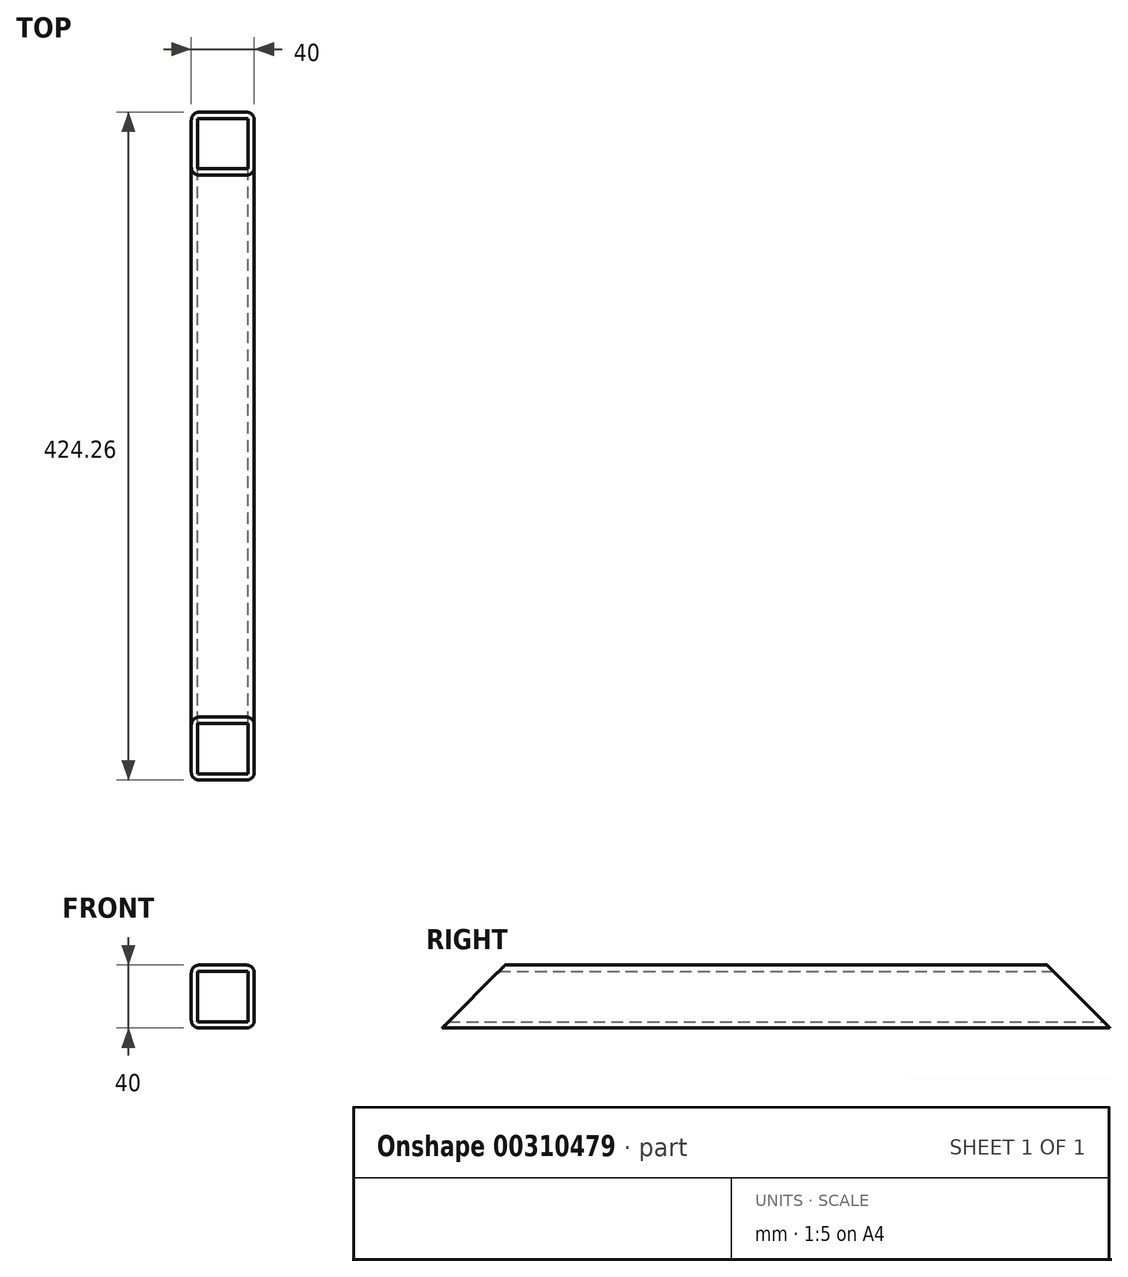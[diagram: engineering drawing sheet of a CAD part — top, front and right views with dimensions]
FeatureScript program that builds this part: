
annotation { "Feature Type Name" : "Feature", "Feature Type Description" : "" }
export const myFeature = defineFeature(function(context is Context, id is Id, definition is map)
    precondition{}
    {
        {
            var Q0;
            Q0=qCreatedBy(makeId("Front.planeOp"),FACE);
            var sketch = newSketch(context, id + "F0", { "sketchPlane" : qUnion([Q0])});
            skLineSegment(sketch, "E0.bottom", {"start": v(15, -20) * mm, "end": v(-15, -20) * mm});
            skLineSegment(sketch, "E0.top", {"start": v(15, 20) * mm, "end": v(-15, 20) * mm});
            skLineSegment(sketch, "E0.left", {"start": v(20, -15) * mm, "end": v(20, 15) * mm});
            skLineSegment(sketch, "E0.right", {"start": v(-20, -15) * mm, "end": v(-20, 15) * mm});
            skPoint(sketch, "E0.middle", {"position": v(0, 0) * mm});
            skPoint(sketch, "E1.visualSharp", {"position": v(-20, 20) * mm});
            skArc(sketch, "E1.filletArc", {"start": v(-15, 20) * mm, "mid": v(-18.54, 18.54) * mm, "end": v(-20, 15) * mm});
            skPoint(sketch, "E2.visualSharp", {"position": v(20, 20) * mm});
            skArc(sketch, "E2.filletArc", {"start": v(20, 15) * mm, "mid": v(18.54, 18.54) * mm, "end": v(15, 20) * mm});
            skPoint(sketch, "E3.visualSharp", {"position": v(20, -20) * mm});
            skArc(sketch, "E3.filletArc", {"start": v(15, -20) * mm, "mid": v(18.54, -18.54) * mm, "end": v(20, -15) * mm});
            skPoint(sketch, "E4.visualSharp", {"position": v(-20, -20) * mm});
            skArc(sketch, "E4.filletArc", {"start": v(-20, -15) * mm, "mid": v(-18.54, -18.54) * mm, "end": v(-15, -20) * mm});
            skLineSegment(sketch, "E5.0", {"start": v(-16, -16) * mm, "end": v(-16, 16) * mm});
            skLineSegment(sketch, "E5.1", {"start": v(16, -16) * mm, "end": v(-16, -16) * mm});
            skLineSegment(sketch, "E5.2", {"start": v(16, -16) * mm, "end": v(16, 16) * mm});
            skLineSegment(sketch, "E5.3", {"start": v(16, 16) * mm, "end": v(-16, 16) * mm});
            skSolve(sketch);
        }
        {
            var Q0;
            Q0=makeQuery(id+"F0.imprint","IMPRINT",FACE,{"disambiguationData":[TD([[makeQuery(id+"F0.imprint","IMPRINT",EDGE,{"derivedFrom":sQuery(id+"F0.wireOp",EDGE,"E0.bottom")}),-1.0]])]});
            extrude(context, id + "F1", {"entities" : qUnion([Q0]), "depth" : 424.26 * mm});
        }
        {
            var Q0;
            Q0=makeQuery(id+"F1.opExtrude","CAP_FACE",FACE,{"disambiguationData":[OSD([sQuery(id+"F0.wireOp",EDGE,"E0.bottom"),sQuery(id+"F0.wireOp",EDGE,"E0.top"),sQuery(id+"F0.wireOp",EDGE,"E0.left"),sQuery(id+"F0.wireOp",EDGE,"E0.right"),sQuery(id+"F0.wireOp",EDGE,"E1.filletArc"),sQuery(id+"F0.wireOp",EDGE,"E2.filletArc"),sQuery(id+"F0.wireOp",EDGE,"E3.filletArc"),sQuery(id+"F0.wireOp",EDGE,"E4.filletArc"),sQuery(id+"F0.wireOp",EDGE,"E5.0"),sQuery(id+"F0.wireOp",EDGE,"E5.1"),sQuery(id+"F0.wireOp",EDGE,"E5.2"),sQuery(id+"F0.wireOp",EDGE,"E5.3")])],"isStart":false});
            var sketch = newSketch(context, id + "F2", { "sketchPlane" : qUnion([Q0])});
            skLineSegment(sketch, "E6.bottom", {"start": v(20, -20) * mm, "end": v(-20, -20) * mm});
            skLineSegment(sketch, "E6.top", {"start": v(20, 20) * mm, "end": v(-20, 20) * mm});
            skLineSegment(sketch, "E6.left", {"start": v(20, -20) * mm, "end": v(20, 20) * mm});
            skLineSegment(sketch, "E6.right", {"start": v(-20, -20) * mm, "end": v(-20, 20) * mm});
            skPoint(sketch, "E6.middle", {"position": v(0, 0) * mm});
            skLineSegment(sketch, "E7.bottom", {"start": v(-20, -20) * mm, "end": v(20, -20) * mm});
            skLineSegment(sketch, "E7.top", {"start": v(-20, 37) * mm, "end": v(20, 37) * mm});
            skLineSegment(sketch, "E7.left", {"start": v(-20, -20) * mm, "end": v(-20, 37) * mm});
            skLineSegment(sketch, "E7.right", {"start": v(20, -20) * mm, "end": v(20, 37) * mm});
            skSolve(sketch);
        }
        {
            var Q0;
            {var subQ3=makeQuery(id+"F1.opExtrude","CAP_EDGE",EDGE,{"disambiguationData":[OSD([sQuery(id+"F0.wireOp",EDGE,"E1.filletArc")])],"isStart":false});Q0=makeQuery(id+"F2.imprint","IMPRINT",FACE,{"disambiguationData":[TD([[makeQuery(id+"F2.imprint","IMPRINT",EDGE,{"derivedFrom":subQ3}),1.0]])]});}
            var Q1;
            {var subQ1=makeQuery(id+"F1.opExtrude","CAP_EDGE",EDGE,{"disambiguationData":[OSD([sQuery(id+"F0.wireOp",EDGE,"E2.filletArc")])],"isStart":false});Q1=makeQuery(id+"F2.imprint","IMPRINT",FACE,{"disambiguationData":[TD([[makeQuery(id+"F2.imprint","IMPRINT",EDGE,{"derivedFrom":subQ1}),-1.0]])]});}
            var Q2;
            {var subQ1=makeQuery(id+"F1.opExtrude","CAP_EDGE",EDGE,{"disambiguationData":[OSD([sQuery(id+"F0.wireOp",EDGE,"E1.filletArc")])],"isStart":false});Q2=makeQuery(id+"F2.imprint","IMPRINT",FACE,{"disambiguationData":[TD([[makeQuery(id+"F2.imprint","IMPRINT",EDGE,{"derivedFrom":subQ1}),-1.0]])]});}
            var Q3;
            {var subQ1=makeQuery(id+"F1.opExtrude","CAP_EDGE",EDGE,{"disambiguationData":[OSD([sQuery(id+"F0.wireOp",EDGE,"E3.filletArc")])],"isStart":false});Q3=makeQuery(id+"F2.imprint","IMPRINT",FACE,{"disambiguationData":[TD([[makeQuery(id+"F2.imprint","IMPRINT",EDGE,{"derivedFrom":subQ1}),-1.0]])]});}
            var Q4;
            Q4=makeQuery(id+"F2.imprint","IMPRINT",FACE,{"disambiguationData":[TD([[makeQuery(id+"F2.imprint","IMPRINT",EDGE,{"derivedFrom":makeQuery(id+"F1.opExtrude","CAP_EDGE",EDGE,{"disambiguationData":[OSD([sQuery(id+"F0.wireOp",EDGE,"E5.0")])],"isStart":false})}),-1.0]])]});
            var Q5;
            {var subQ4=sQuery(id+"F2.wireOp",EDGE,"E7.top");Q5=makeQuery(id+"F2.imprint","IMPRINT",FACE,{"disambiguationData":[TD([[makeQuery(id+"F2.imprint","IMPRINT",EDGE,{"derivedFrom":subQ4}),-1.0]])]});}
            var Q6;
            {var subQ1=makeQuery(id+"F1.opExtrude","CAP_EDGE",EDGE,{"disambiguationData":[OSD([sQuery(id+"F0.wireOp",EDGE,"E4.filletArc")])],"isStart":false});Q6=makeQuery(id+"F2.imprint","IMPRINT",FACE,{"disambiguationData":[TD([[makeQuery(id+"F2.imprint","IMPRINT",EDGE,{"derivedFrom":subQ1}),-1.0]])]});}
            var Q7;
            Q7=sQuery(id+"F2.wireOp",EDGE,"E7.bottom");
            revolve(context, id + "F3", {"operationType" : NewBodyOperationType.REMOVE, "entities" : qUnion([Q0, Q1, Q2, Q3, Q4, Q5, Q6]), "axis" : qUnion([Q7]), "revolveType" : RevolveType.ONE_DIRECTION, "oppositeDirection" : true, "angle" : 45 * degree});
        }
        {
            var Q0;
            Q0=makeQuery(id+"F1.opExtrude","CAP_FACE",FACE,{"disambiguationData":[OSD([sQuery(id+"F0.wireOp",EDGE,"E0.bottom"),sQuery(id+"F0.wireOp",EDGE,"E0.top"),sQuery(id+"F0.wireOp",EDGE,"E0.left"),sQuery(id+"F0.wireOp",EDGE,"E0.right"),sQuery(id+"F0.wireOp",EDGE,"E1.filletArc"),sQuery(id+"F0.wireOp",EDGE,"E2.filletArc"),sQuery(id+"F0.wireOp",EDGE,"E3.filletArc"),sQuery(id+"F0.wireOp",EDGE,"E4.filletArc"),sQuery(id+"F0.wireOp",EDGE,"E5.0"),sQuery(id+"F0.wireOp",EDGE,"E5.1"),sQuery(id+"F0.wireOp",EDGE,"E5.2"),sQuery(id+"F0.wireOp",EDGE,"E5.3")])],"isStart":true});
            var sketch = newSketch(context, id + "F4", { "sketchPlane" : qUnion([Q0])});
            skLineSegment(sketch, "E8.bottom", {"start": v(-20, -20) * mm, "end": v(20, -20) * mm});
            skLineSegment(sketch, "E8.top", {"start": v(-20, 37) * mm, "end": v(20, 37) * mm});
            skLineSegment(sketch, "E8.left", {"start": v(-20, -20) * mm, "end": v(-20, 37) * mm});
            skLineSegment(sketch, "E8.right", {"start": v(20, -20) * mm, "end": v(20, 37) * mm});
            skSolve(sketch);
        }
        {
            var Q0;
            {var subQ2=sQuery(id+"F4.wireOp",EDGE,"E8.top");Q0=makeQuery(id+"F4.imprint","IMPRINT",FACE,{"disambiguationData":[TD([[makeQuery(id+"F4.imprint","IMPRINT",EDGE,{"derivedFrom":subQ2}),-1.0]])]});}
            var Q1;
            Q1=makeQuery(id+"F4.imprint","IMPRINT",FACE,{"disambiguationData":[TD([[makeQuery(id+"F4.imprint","IMPRINT",EDGE,{"derivedFrom":makeQuery(id+"F1.opExtrude","CAP_EDGE",EDGE,{"disambiguationData":[OSD([sQuery(id+"F0.wireOp",EDGE,"E5.0")])],"isStart":true})}),1.0]])]});
            var Q2;
            Q2=makeQuery(id+"F4.imprint","IMPRINT",FACE,{"disambiguationData":[TD([[makeQuery(id+"F4.imprint","IMPRINT",EDGE,{"derivedFrom":makeQuery(id+"F1.opExtrude","CAP_EDGE",EDGE,{"disambiguationData":[OSD([sQuery(id+"F0.wireOp",EDGE,"E0.top")])],"isStart":true})}),-1.0]])]});
            var Q3;
            {var subQ1=makeQuery(id+"F1.opExtrude","CAP_EDGE",EDGE,{"disambiguationData":[OSD([sQuery(id+"F0.wireOp",EDGE,"E4.filletArc")])],"isStart":true});Q3=makeQuery(id+"F4.imprint","IMPRINT",FACE,{"disambiguationData":[TD([[makeQuery(id+"F4.imprint","IMPRINT",EDGE,{"derivedFrom":subQ1}),1.0]])]});}
            var Q4;
            {var subQ1=makeQuery(id+"F1.opExtrude","CAP_EDGE",EDGE,{"disambiguationData":[OSD([sQuery(id+"F0.wireOp",EDGE,"E3.filletArc")])],"isStart":true});Q4=makeQuery(id+"F4.imprint","IMPRINT",FACE,{"disambiguationData":[TD([[makeQuery(id+"F4.imprint","IMPRINT",EDGE,{"derivedFrom":subQ1}),1.0]])]});}
            var Q5;
            Q5=sQuery(id+"F4.wireOp",EDGE,"E8.bottom");
            revolve(context, id + "F5", {"operationType" : NewBodyOperationType.REMOVE, "entities" : qUnion([Q0, Q1, Q2, Q3, Q4]), "axis" : qUnion([Q5]), "revolveType" : RevolveType.ONE_DIRECTION, "oppositeDirection" : true, "angle" : 45 * degree});
        }
    });
